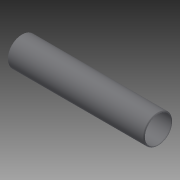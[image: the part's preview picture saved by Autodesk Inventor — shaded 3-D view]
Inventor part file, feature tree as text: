
AUTODESK INVENTOR PART (.ipt)
format: ipt  version: 2014 (Build 180170000, 170)  size: 145,920 bytes
history: native  units: in
note: dims shown in document units (in); Inventor stores cm internally (conversion verified against a paired STEP export)
features: other x42, revolve x1, sketch x1
ambient origin geometry x8: Origin, YZ Plane, XZ Plane, XY Plane, X Axis, Y Axis, Z Axis, Center Point
bodies: Solid1 (feature_tree)
feature tree (44):
  revolve  "Revolution1"  [1 undecoded]
  other  "cp1_XY"
  other  "cp1_YZ"
  other  "cp1_ZX"
  other  "cp1_X"
  other  "cp1_Y"
  other  "cp1_Z"
  other  "cp1_Center"
  other  "cp2_XY"
  other  "cp2_YZ"
  other  "cp2_ZX"
  other  "cp2_X"
  other  "cp2_Y"
  other  "cp2_Z"
  other  "cp2_Center"
  other  "cp3_XY"
  other  "cp3_YZ"
  other  "cp3_ZX"
  other  "cp3_X"
  other  "cp3_Y"
  other  "cp3_Z"
  other  "cp3_Center"
  other  "cp4_XY"
  other  "cp4_YZ"
  other  "cp4_ZX"
  other  "cp4_X"
  other  "cp4_Y"
  other  "cp4_Z"
  other  "cp4_Center"
  other  "tube_front_XY"
  other  "tube_front_YZ"
  other  "tube_front_ZX"
  other  "tube_front_X"
  other  "tube_front_Y"
  other  "tube_front_Z"
  other  "tube_front_Center"
  other  "tube_rear_XY"
  other  "tube_rear_YZ"
  other  "tube_rear_ZX"
  other  "tube_rear_X"
  other  "tube_rear_Y"
  other  "tube_rear_Z"
  other  "tube_rear_Center"
  sketch  "Sketch_1"  dims[d0=360.0deg]
note: 1 required parameter value undecoded (feature->parameter linkage not recoverable at this tier; creation-order binding heuristic only, values carry confidence <= 0.55)
